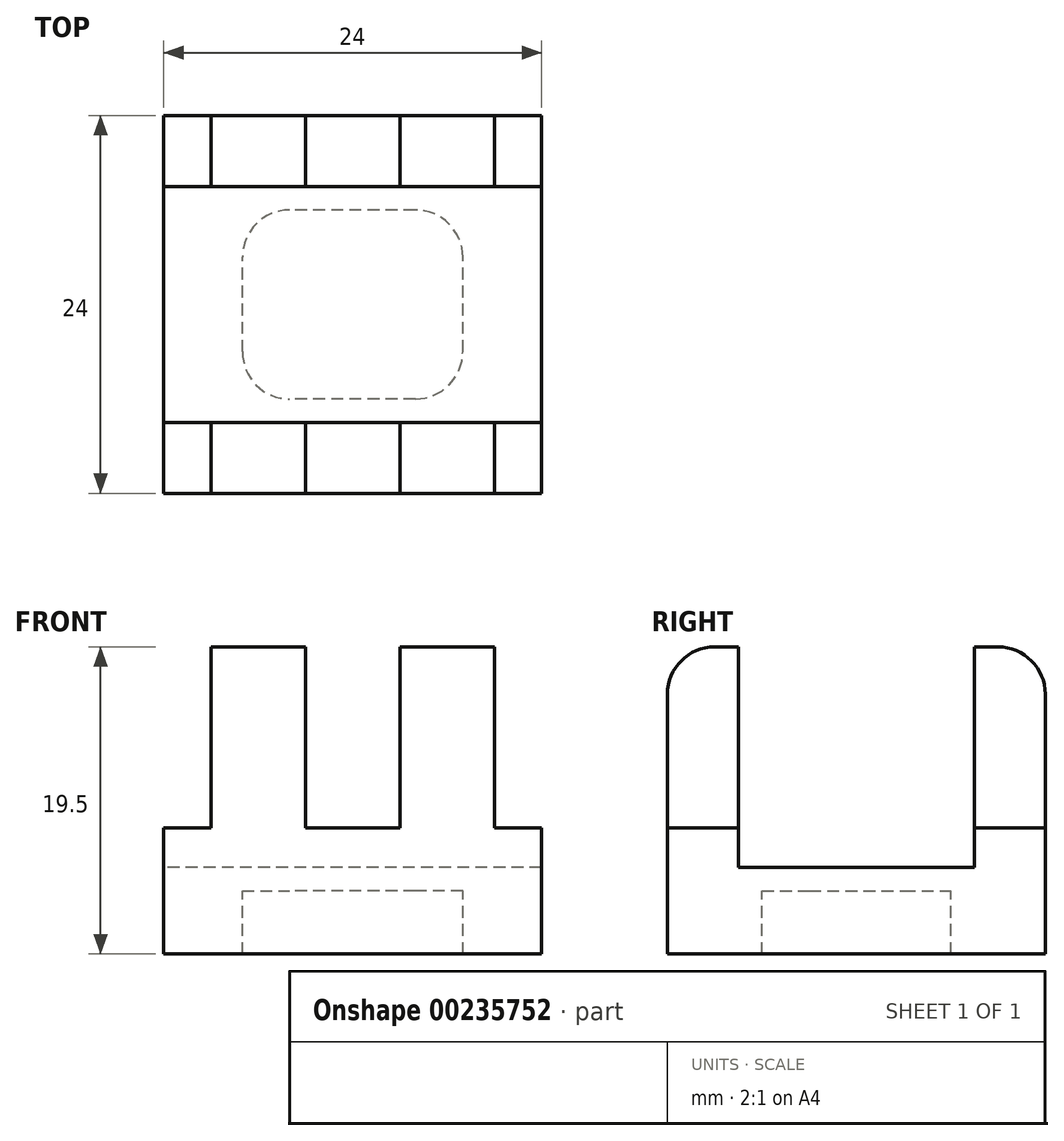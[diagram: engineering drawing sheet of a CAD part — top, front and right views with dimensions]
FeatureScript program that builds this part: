
annotation { "Feature Type Name" : "Feature", "Feature Type Description" : "" }
export const myFeature = defineFeature(function(context is Context, id is Id, definition is map)
    precondition{}
    {
        {
            var Q0;
            Q0=qCreatedBy(makeId("Top.planeOp"),FACE);
            var sketch = newSketch(context, id + "F0", { "sketchPlane" : qUnion([Q0])});
            skLineSegment(sketch, "E0.bottom", {"start": v(12, 12) * mm, "end": v(-12, 12) * mm});
            skLineSegment(sketch, "E0.top", {"start": v(12, -12) * mm, "end": v(-12, -12) * mm});
            skLineSegment(sketch, "E0.left", {"start": v(12, 12) * mm, "end": v(12, -12) * mm});
            skLineSegment(sketch, "E0.right", {"start": v(-12, 12) * mm, "end": v(-12, -12) * mm});
            skPoint(sketch, "E0.middle", {"position": v(0, 0) * mm});
            skLineSegment(sketch, "E1.bottom", {"start": v(4, -6) * mm, "end": v(-4, -6) * mm});
            skLineSegment(sketch, "E1.top", {"start": v(4, 6) * mm, "end": v(-4, 6) * mm});
            skLineSegment(sketch, "E1.left", {"start": v(7, -3) * mm, "end": v(7, 3) * mm});
            skLineSegment(sketch, "E1.right", {"start": v(-7, -3) * mm, "end": v(-7, 3) * mm});
            skLineSegment(sketch, "E2.bottom", {"start": v(12, -7.5) * mm, "end": v(-12, -7.5) * mm});
            skLineSegment(sketch, "E2.top", {"start": v(12, 7.5) * mm, "end": v(-12, 7.5) * mm});
            skLineSegment(sketch, "E2.left", {"start": v(12, -7.5) * mm, "end": v(12, 7.5) * mm, "construction": true});
            skLineSegment(sketch, "E2.right", {"start": v(-12, -7.5) * mm, "end": v(-12, 7.5) * mm, "construction": true});
            skLineSegment(sketch, "E3.bottom", {"start": v(3, -12) * mm, "end": v(-3, -12) * mm, "construction": true});
            skLineSegment(sketch, "E3.top", {"start": v(3, 12) * mm, "end": v(-3, 12) * mm, "construction": true});
            skLineSegment(sketch, "E3.left", {"start": v(3, -12) * mm, "end": v(3, -7.5) * mm});
            skLineSegment(sketch, "E3.right", {"start": v(-3, -12) * mm, "end": v(-3, -7.5) * mm});
            skLineSegment(sketch, "E4.bottom", {"start": v(9, -12) * mm, "end": v(-9, -12) * mm, "construction": true});
            skLineSegment(sketch, "E4.top", {"start": v(9, 12) * mm, "end": v(-9, 12) * mm, "construction": true});
            skLineSegment(sketch, "E4.left", {"start": v(9, -12) * mm, "end": v(9, -7.5) * mm});
            skLineSegment(sketch, "E4.right", {"start": v(-9, -12) * mm, "end": v(-9, -7.5) * mm});
            skLineSegment(sketch, "E5.trimOffspring", {"start": v(-9, 7.5) * mm, "end": v(-9, 12) * mm});
            skLineSegment(sketch, "E6.trimOffspring", {"start": v(-3, 7.5) * mm, "end": v(-3, 12) * mm});
            skLineSegment(sketch, "E7.trimOffspring", {"start": v(3, 7.5) * mm, "end": v(3, 12) * mm});
            skLineSegment(sketch, "E8.trimOffspring", {"start": v(9, 7.5) * mm, "end": v(9, 12) * mm});
            skPoint(sketch, "E9.visualSharp", {"position": v(-7, 6) * mm});
            skArc(sketch, "E9.filletArc", {"start": v(-4, 6) * mm, "mid": v(-6.12, 5.12) * mm, "end": v(-7, 3) * mm});
            skPoint(sketch, "E10.visualSharp", {"position": v(7, 6) * mm});
            skArc(sketch, "E10.filletArc", {"start": v(7, 3) * mm, "mid": v(6.12, 5.12) * mm, "end": v(4, 6) * mm});
            skPoint(sketch, "E11.visualSharp", {"position": v(7, -6) * mm});
            skArc(sketch, "E11.filletArc", {"start": v(4, -6) * mm, "mid": v(6.12, -5.12) * mm, "end": v(7, -3) * mm});
            skPoint(sketch, "E12.visualSharp", {"position": v(-7, -6) * mm});
            skArc(sketch, "E12.filletArc", {"start": v(-7, -3) * mm, "mid": v(-6.12, -5.12) * mm, "end": v(-4, -6) * mm});
            skSolve(sketch);
        }
        {
            var Q0;
            Q0=makeQuery(id+"F0.imprint","IMPRINT",FACE,{"disambiguationData":[TD([[makeQuery(id+"F0.imprint","IMPRINT",EDGE,{"derivedFrom":sQuery(id+"F0.wireOp",EDGE,"E1.bottom")}),1.0]])]});
            var Q1;
            {var subQ3=sQuery(id+"F0.wireOp",EDGE,"E4.left");Q1=makeQuery(id+"F0.imprint","IMPRINT",FACE,{"disambiguationData":[TD([[makeQuery(id+"F0.imprint","IMPRINT",EDGE,{"derivedFrom":subQ3}),-1.0]])]});}
            var Q2;
            {var subQ0=sQuery(id+"F0.wireOp",EDGE,"E3.left");Q2=makeQuery(id+"F0.imprint","IMPRINT",FACE,{"disambiguationData":[TD([[makeQuery(id+"F0.imprint","IMPRINT",EDGE,{"derivedFrom":subQ0}),-1.0]])]});}
            var Q3;
            {var subQ0=sQuery(id+"F0.wireOp",EDGE,"E3.left");Q3=makeQuery(id+"F0.imprint","IMPRINT",FACE,{"disambiguationData":[TD([[makeQuery(id+"F0.imprint","IMPRINT",EDGE,{"derivedFrom":subQ0}),1.0]])]});}
            var Q4;
            {var subQ0=sQuery(id+"F0.wireOp",EDGE,"E3.right");Q4=makeQuery(id+"F0.imprint","IMPRINT",FACE,{"disambiguationData":[TD([[makeQuery(id+"F0.imprint","IMPRINT",EDGE,{"derivedFrom":subQ0}),1.0]])]});}
            var Q5;
            {var subQ3=sQuery(id+"F0.wireOp",EDGE,"E4.right");Q5=makeQuery(id+"F0.imprint","IMPRINT",FACE,{"disambiguationData":[TD([[makeQuery(id+"F0.imprint","IMPRINT",EDGE,{"derivedFrom":subQ3}),1.0]])]});}
            var Q6;
            {var subQ3=sQuery(id+"F0.wireOp",EDGE,"E5.trimOffspring");Q6=makeQuery(id+"F0.imprint","IMPRINT",FACE,{"disambiguationData":[TD([[makeQuery(id+"F0.imprint","IMPRINT",EDGE,{"derivedFrom":subQ3}),1.0]])]});}
            var Q7;
            {var subQ0=sQuery(id+"F0.wireOp",EDGE,"E5.trimOffspring");Q7=makeQuery(id+"F0.imprint","IMPRINT",FACE,{"disambiguationData":[TD([[makeQuery(id+"F0.imprint","IMPRINT",EDGE,{"derivedFrom":subQ0}),-1.0]])]});}
            var Q8;
            {var subQ0=sQuery(id+"F0.wireOp",EDGE,"E6.trimOffspring");Q8=makeQuery(id+"F0.imprint","IMPRINT",FACE,{"disambiguationData":[TD([[makeQuery(id+"F0.imprint","IMPRINT",EDGE,{"derivedFrom":subQ0}),-1.0]])]});}
            var Q9;
            {var subQ0=sQuery(id+"F0.wireOp",EDGE,"E7.trimOffspring");Q9=makeQuery(id+"F0.imprint","IMPRINT",FACE,{"disambiguationData":[TD([[makeQuery(id+"F0.imprint","IMPRINT",EDGE,{"derivedFrom":subQ0}),-1.0]])]});}
            var Q10;
            {var subQ3=sQuery(id+"F0.wireOp",EDGE,"E8.trimOffspring");Q10=makeQuery(id+"F0.imprint","IMPRINT",FACE,{"disambiguationData":[TD([[makeQuery(id+"F0.imprint","IMPRINT",EDGE,{"derivedFrom":subQ3}),-1.0]])]});}
            extrude(context, id + "F1", {"entities" : qUnion([Q0, Q1, Q2, Q3, Q4, Q5, Q6, Q7, Q8, Q9, Q10]), "oppositeDirection" : true, "depth" : 4 * mm});
        }
        {
            var Q0;
            Q0=makeQuery(id+"F0.imprint","IMPRINT",FACE,{"disambiguationData":[TD([[makeQuery(id+"F0.imprint","IMPRINT",EDGE,{"derivedFrom":sQuery(id+"F0.wireOp",EDGE,"E1.bottom")}),1.0]])]});
            var Q1;
            Q1=makeQuery(id+"F0.imprint","IMPRINT",FACE,{"disambiguationData":[TD([[makeQuery(id+"F0.imprint","IMPRINT",EDGE,{"derivedFrom":sQuery(id+"F0.wireOp",EDGE,"E1.bottom")}),-1.0]])]});
            extrude(context, id + "F2", {"entities" : qUnion([Q0, Q1]), "operationType" : NewBodyOperationType.ADD, "depth" : 1.5 * mm});
        }
        {
            var Q0;
            {var subQ3=sQuery(id+"F0.wireOp",EDGE,"E8.trimOffspring");Q0=makeQuery(id+"F0.imprint","IMPRINT",FACE,{"disambiguationData":[TD([[makeQuery(id+"F0.imprint","IMPRINT",EDGE,{"derivedFrom":subQ3}),-1.0]])]});}
            var Q1;
            {var subQ0=sQuery(id+"F0.wireOp",EDGE,"E6.trimOffspring");Q1=makeQuery(id+"F0.imprint","IMPRINT",FACE,{"disambiguationData":[TD([[makeQuery(id+"F0.imprint","IMPRINT",EDGE,{"derivedFrom":subQ0}),-1.0]])]});}
            var Q2;
            {var subQ3=sQuery(id+"F0.wireOp",EDGE,"E5.trimOffspring");Q2=makeQuery(id+"F0.imprint","IMPRINT",FACE,{"disambiguationData":[TD([[makeQuery(id+"F0.imprint","IMPRINT",EDGE,{"derivedFrom":subQ3}),1.0]])]});}
            var Q3;
            {var subQ3=sQuery(id+"F0.wireOp",EDGE,"E4.right");Q3=makeQuery(id+"F0.imprint","IMPRINT",FACE,{"disambiguationData":[TD([[makeQuery(id+"F0.imprint","IMPRINT",EDGE,{"derivedFrom":subQ3}),1.0]])]});}
            var Q4;
            {var subQ0=sQuery(id+"F0.wireOp",EDGE,"E3.left");Q4=makeQuery(id+"F0.imprint","IMPRINT",FACE,{"disambiguationData":[TD([[makeQuery(id+"F0.imprint","IMPRINT",EDGE,{"derivedFrom":subQ0}),1.0]])]});}
            var Q5;
            {var subQ3=sQuery(id+"F0.wireOp",EDGE,"E4.left");Q5=makeQuery(id+"F0.imprint","IMPRINT",FACE,{"disambiguationData":[TD([[makeQuery(id+"F0.imprint","IMPRINT",EDGE,{"derivedFrom":subQ3}),-1.0]])]});}
            extrude(context, id + "F3", {"entities" : qUnion([Q0, Q1, Q2, Q3, Q4, Q5]), "operationType" : NewBodyOperationType.ADD, "depth" : 4 * mm});
        }
        {
            var Q0;
            {var subQ0=sQuery(id+"F0.wireOp",EDGE,"E5.trimOffspring");Q0=makeQuery(id+"F0.imprint","IMPRINT",FACE,{"disambiguationData":[TD([[makeQuery(id+"F0.imprint","IMPRINT",EDGE,{"derivedFrom":subQ0}),-1.0]])]});}
            var Q1;
            {var subQ0=sQuery(id+"F0.wireOp",EDGE,"E7.trimOffspring");Q1=makeQuery(id+"F0.imprint","IMPRINT",FACE,{"disambiguationData":[TD([[makeQuery(id+"F0.imprint","IMPRINT",EDGE,{"derivedFrom":subQ0}),-1.0]])]});}
            var Q2;
            {var subQ0=sQuery(id+"F0.wireOp",EDGE,"E3.left");Q2=makeQuery(id+"F0.imprint","IMPRINT",FACE,{"disambiguationData":[TD([[makeQuery(id+"F0.imprint","IMPRINT",EDGE,{"derivedFrom":subQ0}),-1.0]])]});}
            var Q3;
            {var subQ0=sQuery(id+"F0.wireOp",EDGE,"E3.right");Q3=makeQuery(id+"F0.imprint","IMPRINT",FACE,{"disambiguationData":[TD([[makeQuery(id+"F0.imprint","IMPRINT",EDGE,{"derivedFrom":subQ0}),1.0]])]});}
            extrude(context, id + "F4", {"entities" : qUnion([Q0, Q1, Q2, Q3]), "operationType" : NewBodyOperationType.ADD, "depth" : 15.5 * mm});
        }
        {
            var Q0;
            {var subQ0=sQuery(id+"F0.wireOp",EDGE,"E0.bottom");Q0=makeQuery(id+"F4.opExtrude","CAP_EDGE",EDGE,{"disambiguationData":[OSD([subQ0]),TDD([makeQuery(id+"F0.imprint","IMPRINT",EDGE,{"disambiguationData":[TD([[makeQuery(id+"F0.imprint","INTERSECT",VERTEX,{"derivedFrom":[subQ0,sQuery(id+"F0.wireOp",EDGE,"E7.trimOffspring")]}),1.0]])],"derivedFrom":subQ0})])],"isStart":false});}
            var Q1;
            {var subQ0=sQuery(id+"F0.wireOp",EDGE,"E0.bottom");Q1=makeQuery(id+"F4.opExtrude","CAP_EDGE",EDGE,{"disambiguationData":[OSD([subQ0]),TDD([makeQuery(id+"F0.imprint","IMPRINT",EDGE,{"disambiguationData":[TD([[makeQuery(id+"F0.imprint","INTERSECT",VERTEX,{"derivedFrom":[subQ0,sQuery(id+"F0.wireOp",EDGE,"E5.trimOffspring")]}),1.0]])],"derivedFrom":subQ0})])],"isStart":false});}
            var Q2;
            {var subQ0=sQuery(id+"F0.wireOp",EDGE,"E0.top");Q2=makeQuery(id+"F4.opExtrude","CAP_EDGE",EDGE,{"disambiguationData":[OSD([subQ0]),TDD([makeQuery(id+"F0.imprint","IMPRINT",EDGE,{"disambiguationData":[TD([[makeQuery(id+"F0.imprint","INTERSECT",VERTEX,{"derivedFrom":[subQ0,sQuery(id+"F0.wireOp",EDGE,"E3.left")]}),1.0]])],"derivedFrom":subQ0})])],"isStart":false});}
            var Q3;
            {var subQ0=sQuery(id+"F0.wireOp",EDGE,"E0.top");Q3=makeQuery(id+"F4.opExtrude","CAP_EDGE",EDGE,{"disambiguationData":[OSD([subQ0]),TDD([makeQuery(id+"F0.imprint","IMPRINT",EDGE,{"disambiguationData":[TD([[makeQuery(id+"F0.imprint","INTERSECT",VERTEX,{"derivedFrom":[subQ0,sQuery(id+"F0.wireOp",EDGE,"E3.right")]}),-1.0]])],"derivedFrom":subQ0})])],"isStart":false});}
            fillet(context, id + "F5", {"entities" : qUnion([Q0, Q1, Q2, Q3]), "radius" : 3 * mm, "tangentPropagation" : true, "allowEdgeOverflow" : false});
        }
    });
